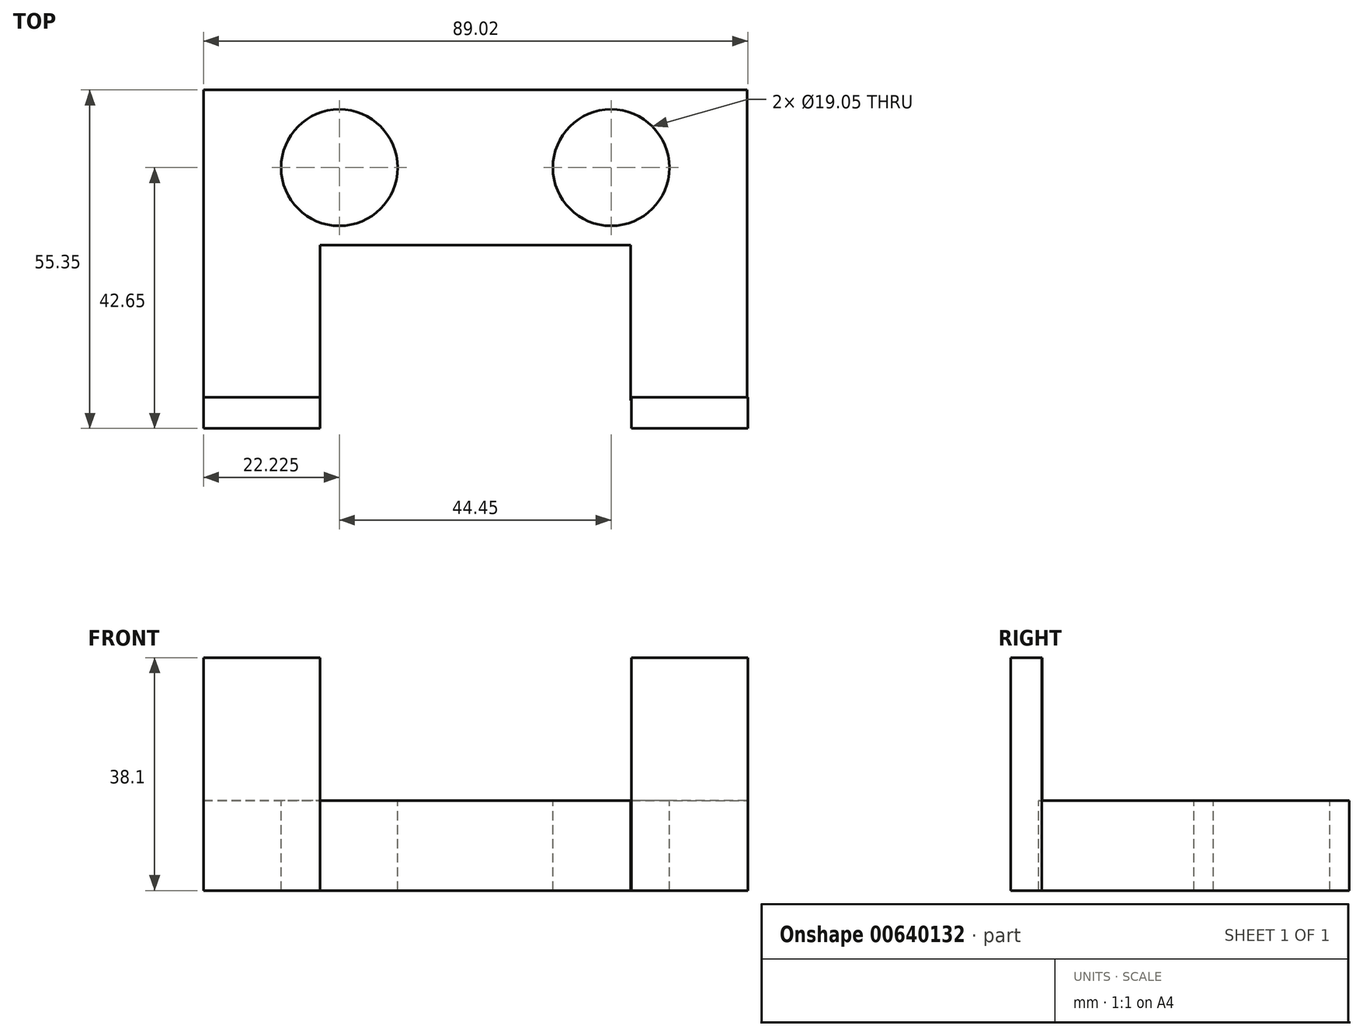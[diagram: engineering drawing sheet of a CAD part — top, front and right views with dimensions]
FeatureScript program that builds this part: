
annotation { "Feature Type Name" : "Feature", "Feature Type Description" : "" }
export const myFeature = defineFeature(function(context is Context, id is Id, definition is map)
    precondition{}
    {
        {
            var Q0;
            Q0=qCreatedBy(makeId("Top.planeOp"),FACE);
            var sketch = newSketch(context, id + "F0", { "sketchPlane" : qUnion([Q0])});
            skLineSegment(sketch, "E0.bottom", {"start": v(44.45, 25.4) * mm, "end": v(-44.45, 25.4) * mm});
            skLineSegment(sketch, "E0.top", {"start": v(44.45, -25.4) * mm, "end": v(-44.45, -25.4) * mm});
            skLineSegment(sketch, "E0.left", {"start": v(44.45, 25.4) * mm, "end": v(44.45, -25.4) * mm});
            skLineSegment(sketch, "E0.right", {"start": v(-44.45, 25.4) * mm, "end": v(-44.45, -25.4) * mm});
            skPoint(sketch, "E0.middle", {"position": v(0, 0) * mm});
            skSolve(sketch);
        }
        {
            var Q0;
            Q0 = qSketchRegion(id + "F0", true);
            extrude(context, id + "F1", {"entities" : qUnion([Q0]), "depth" : 14.73 * mm, "offsetDistance" : 25.4 * mm});
        }
        {
            var Q0;
            Q0=makeQuery(id+"F1.opExtrude","CAP_FACE",FACE,{"disambiguationData":[OSD([sQuery(id+"F0.wireOp",EDGE,"E0.bottom"),sQuery(id+"F0.wireOp",EDGE,"E0.top"),sQuery(id+"F0.wireOp",EDGE,"E0.left"),sQuery(id+"F0.wireOp",EDGE,"E0.right")])],"isStart":false});
            var sketch = newSketch(context, id + "F2", { "sketchPlane" : qUnion([Q0])});
            skLineSegment(sketch, "E1.bottom", {"start": v(25.4, 0) * mm, "end": v(-25.4, 0) * mm});
            skLineSegment(sketch, "E1.top", {"start": v(25.4, -25.4) * mm, "end": v(-25.4, -25.4) * mm});
            skLineSegment(sketch, "E1.left", {"start": v(25.4, 0) * mm, "end": v(25.4, -25.4) * mm});
            skLineSegment(sketch, "E1.right", {"start": v(-25.4, 0) * mm, "end": v(-25.4, -25.4) * mm});
            skPoint(sketch, "E1.middle", {"position": v(0, -12.7) * mm});
            skSolve(sketch);
        }
        {
            var Q0;
            Q0 = qSketchRegion(id + "F2", true);
            extrude(context, id + "F3", {"entities" : qUnion([Q0]), "operationType" : NewBodyOperationType.REMOVE, "oppositeDirection" : true, "depth" : 25.4 * mm, "offsetDistance" : 25.4 * mm});
        }
        {
            var Q0;
            Q0=makeQuery(id+"F1.opExtrude","CAP_FACE",FACE,{"disambiguationData":[OSD([sQuery(id+"F0.wireOp",EDGE,"E0.bottom"),sQuery(id+"F0.wireOp",EDGE,"E0.top"),sQuery(id+"F0.wireOp",EDGE,"E0.left"),sQuery(id+"F0.wireOp",EDGE,"E0.right")])],"isStart":false});
            var sketch = newSketch(context, id + "F4", { "sketchPlane" : qUnion([Q0])});
            skCircle(sketch, "E2", {"center": v(-22.22, 12.7) * mm, "radius": 9.53 * mm});
            skCircle(sketch, "E3", {"center": v(22.23, 12.7) * mm, "radius": 9.53 * mm});
            skSolve(sketch);
        }
        {
            var Q0;
            Q0=qCreatedBy(makeId("Top.planeOp"),FACE);
            var sketch = newSketch(context, id + "F5", { "sketchPlane" : qUnion([Q0])});
            skLineSegment(sketch, "E4.bottom", {"start": v(-25.4, -24.86) * mm, "end": v(-44.45, -24.86) * mm});
            skLineSegment(sketch, "E4.top", {"start": v(-25.4, -29.94) * mm, "end": v(-44.45, -29.94) * mm});
            skLineSegment(sketch, "E4.left", {"start": v(-25.4, -24.86) * mm, "end": v(-25.4, -29.94) * mm});
            skLineSegment(sketch, "E4.right", {"start": v(-44.45, -24.86) * mm, "end": v(-44.45, -29.94) * mm});
            skPoint(sketch, "E4.middle", {"position": v(-34.92, -27.4) * mm});
            skLineSegment(sketch, "E5.bottom", {"start": v(44.57, -24.87) * mm, "end": v(25.52, -24.87) * mm});
            skLineSegment(sketch, "E5.top", {"start": v(44.57, -29.95) * mm, "end": v(25.52, -29.95) * mm});
            skLineSegment(sketch, "E5.left", {"start": v(44.57, -24.87) * mm, "end": v(44.57, -29.95) * mm});
            skLineSegment(sketch, "E5.right", {"start": v(25.52, -24.87) * mm, "end": v(25.52, -29.95) * mm});
            skPoint(sketch, "E5.middle", {"position": v(35.04, -27.4) * mm});
            skSolve(sketch);
        }
        {
            var Q0;
            Q0=makeQuery(id+"F5.imprint","IMPRINT",FACE,{"disambiguationData":[TD([[makeQuery(id+"F5.imprint","IMPRINT",EDGE,{"derivedFrom":sQuery(id+"F5.wireOp",EDGE,"E5.bottom")}),1.0]])]});
            var Q1;
            Q1=makeQuery(id+"F5.imprint","IMPRINT",FACE,{"disambiguationData":[TD([[makeQuery(id+"F5.imprint","IMPRINT",EDGE,{"derivedFrom":sQuery(id+"F5.wireOp",EDGE,"E4.bottom")}),1.0]])]});
            extrude(context, id + "F6", {"entities" : qUnion([Q0, Q1]), "operationType" : NewBodyOperationType.ADD, "depth" : 38.1 * mm, "offsetDistance" : 25.4 * mm});
        }
        {
            var Q0;
            Q0=makeQuery(id+"F4.imprint","IMPRINT",FACE,{"disambiguationData":[TD([[makeQuery(id+"F4.imprint","IMPRINT",EDGE,{"derivedFrom":sQuery(id+"F4.wireOp",EDGE,"E2")}),1.0]])]});
            var Q1;
            Q1=makeQuery(id+"F4.imprint","IMPRINT",FACE,{"disambiguationData":[TD([[makeQuery(id+"F4.imprint","IMPRINT",EDGE,{"derivedFrom":sQuery(id+"F4.wireOp",EDGE,"E3")}),1.0]])]});
            extrude(context, id + "F7", {"entities" : qUnion([Q0, Q1]), "operationType" : NewBodyOperationType.REMOVE, "oppositeDirection" : true, "depth" : 25.4 * mm, "offsetDistance" : 25.4 * mm});
        }
    });
